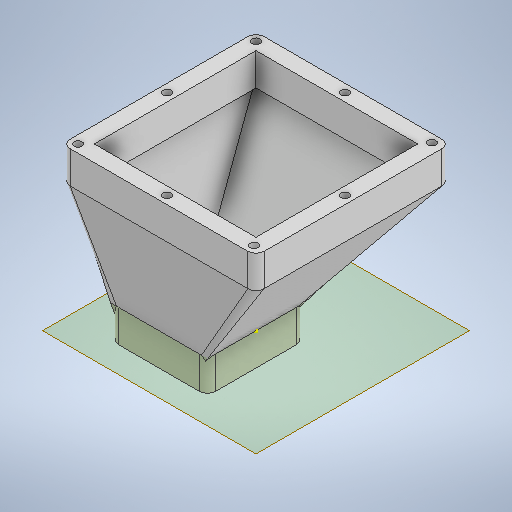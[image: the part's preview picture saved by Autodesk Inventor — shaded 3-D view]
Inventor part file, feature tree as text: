
AUTODESK INVENTOR PART (.ipt)
format: ipt  version: 2025.1 (Build 291241020, 241B)  size: 363,520 bytes
history: native  units: in
note: dims shown in document units (in); Inventor stores cm internally (conversion verified against a paired STEP export)
features: sketch x6, extrude x3, fillet x2, plane x1, loft x1, shell x1, hole x1, other x1
ambient origin geometry x8: Origin, YZ Plane, XZ Plane, XY Plane, X Axis, Y Axis, Z Axis, Center Point
bodies: Solid1 (feature_tree)
feature tree (16):
  extrude  "Extrusion1"  Depth=6.0in
  fillet  "Fillet1"  Radius=5.0in
  plane  "Work Plane1"
  loft  "Loft1"
  sketch  "Sketch3"  dims[d8=1.5in d9=3.0in]
  shell  "Shell3"  Thickness=4.0in
  extrude  "Extrusion2"  Depth=3.0in
  hole  "Hole1"  [1 undecoded]
  fillet  "Fillet2"  [1 undecoded]
  extrude  "Extrusion4"  Depth=0.25in
  sketch  "Sketch1"  dims[d0=6.0in d1=6.0in d2=5.0in]
  sketch  "Sketch2"  dims[d3=1.0in d4=0.0in d5=0.25in d6=4.0in]
  other  "Edges1"
  sketch  "Sketch4"  dims[d10=3.0in d13=0.0in d14=90.0deg d15=0.0in d16=90.0deg]
  sketch  "Sketch7"  dims[d19=1.0in d20=0.0in d27=0.25in]
  sketch  "Sketch8"  dims[d28=2.4in d29=1.5in d30=2.4in d31=0.75in d32=0.375in d33=0.25in d34=0.5635in d35=5.0in d36=0.0in d37=0.25in d38=0.25in d39=0.25in d40=0.25in d41=0.5in d42=0.0in]
note: 2 required parameter values undecoded (feature->parameter linkage not recoverable at this tier; creation-order binding heuristic only, values carry confidence <= 0.55)
